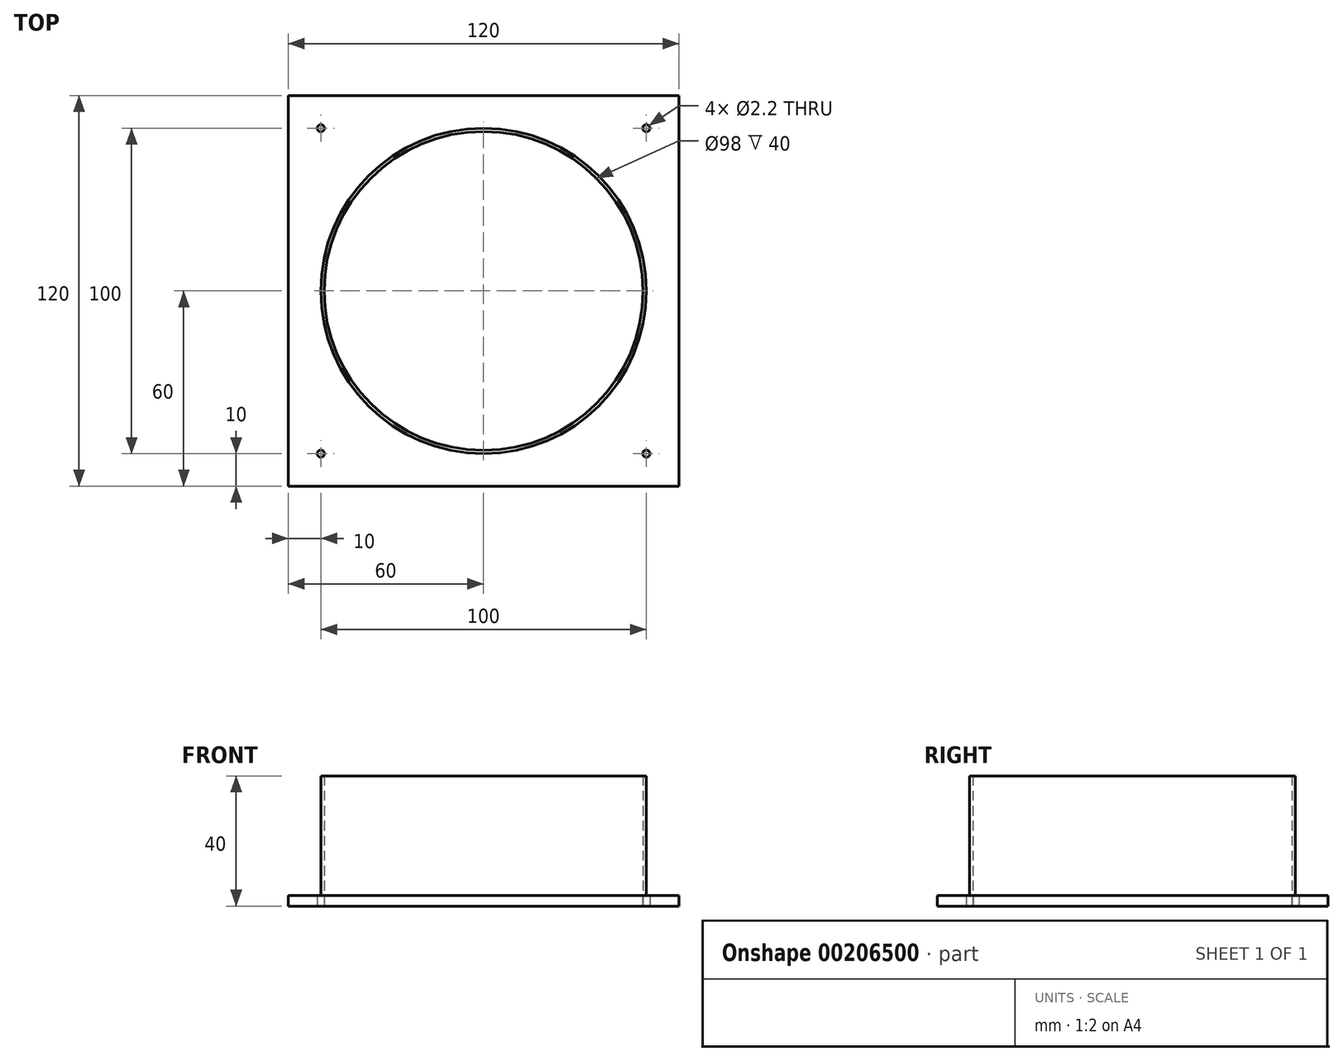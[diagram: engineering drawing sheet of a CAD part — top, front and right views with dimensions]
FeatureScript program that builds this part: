
annotation { "Feature Type Name" : "Feature", "Feature Type Description" : "" }
export const myFeature = defineFeature(function(context is Context, id is Id, definition is map)
    precondition{}
    {
        {
            var Q0;
            Q0=qCreatedBy(makeId("Top.planeOp"),FACE);
            var sketch = newSketch(context, id + "F0", { "sketchPlane" : qUnion([Q0])});
            skCircle(sketch, "E0", {"center": v(0, 0) * mm, "radius": 50 * mm});
            skLineSegment(sketch, "E1.bottom", {"start": v(60, -60) * mm, "end": v(-60, -60) * mm});
            skLineSegment(sketch, "E1.top", {"start": v(60, 60) * mm, "end": v(-60, 60) * mm});
            skLineSegment(sketch, "E1.left", {"start": v(60, -60) * mm, "end": v(60, 60) * mm});
            skLineSegment(sketch, "E1.right", {"start": v(-60, -60) * mm, "end": v(-60, 60) * mm});
            skCircle(sketch, "E2", {"center": v(0, 0) * mm, "radius": 49 * mm});
            skCircle(sketch, "E3", {"center": v(50, 50) * mm, "radius": 1.1 * mm});
            skCircle(sketch, "E4", {"center": v(-50, 50) * mm, "radius": 1.1 * mm});
            skCircle(sketch, "E5", {"center": v(-50, -50) * mm, "radius": 1.1 * mm});
            skCircle(sketch, "E6", {"center": v(50, -50) * mm, "radius": 1.1 * mm});
            skSolve(sketch);
        }
        {
            var Q0;
            Q0=makeQuery(id+"F0.imprint","IMPRINT",FACE,{"disambiguationData":[TD([[makeQuery(id+"F0.imprint","IMPRINT",EDGE,{"derivedFrom":sQuery(id+"F0.wireOp",EDGE,"E0")}),-1.0]])]});
            extrude(context, id + "F1", {"entities" : qUnion([Q0]), "depth" : 3.2 * mm});
        }
        {
            var Q0;
            Q0=makeQuery(id+"F0.imprint","IMPRINT",FACE,{"disambiguationData":[TD([[makeQuery(id+"F0.imprint","IMPRINT",EDGE,{"derivedFrom":sQuery(id+"F0.wireOp",EDGE,"E0")}),1.0]])]});
            extrude(context, id + "F2", {"entities" : qUnion([Q0]), "operationType" : NewBodyOperationType.ADD, "depth" : 40 * mm});
        }
    });
